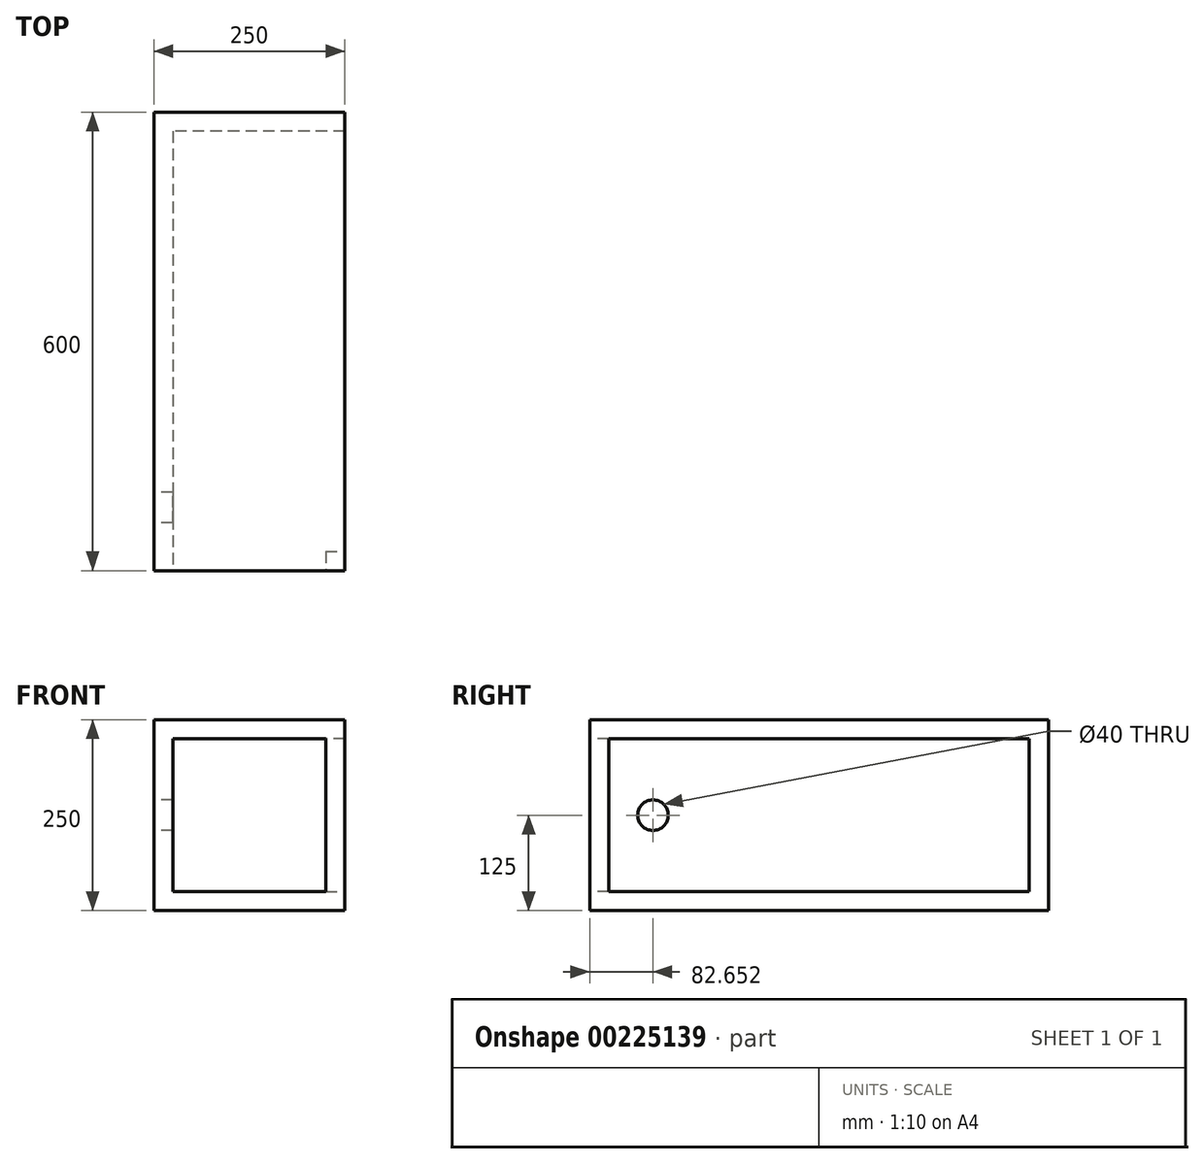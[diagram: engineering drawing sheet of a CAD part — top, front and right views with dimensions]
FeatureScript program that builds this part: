
annotation { "Feature Type Name" : "Feature", "Feature Type Description" : "" }
export const myFeature = defineFeature(function(context is Context, id is Id, definition is map)
    precondition{}
    {
        {
            var Q0;
            Q0=qCreatedBy(makeId("Front.planeOp"),FACE);
            var sketch = newSketch(context, id + "F0", { "sketchPlane" : qUnion([Q0])});
            skLineSegment(sketch, "E0.bottom", {"start": v(125, -125) * mm, "end": v(-125, -125) * mm});
            skLineSegment(sketch, "E0.top", {"start": v(125, 125) * mm, "end": v(-125, 125) * mm});
            skLineSegment(sketch, "E0.left", {"start": v(125, -125) * mm, "end": v(125, 125) * mm});
            skLineSegment(sketch, "E0.right", {"start": v(-125, -125) * mm, "end": v(-125, 125) * mm});
            skPoint(sketch, "E0.middle", {"position": v(0, 0) * mm});
            skSolve(sketch);
        }
        {
            var Q0;
            Q0=makeQuery(id+"F0.imprint","IMPRINT",FACE,{"disambiguationData":[TD([[makeQuery(id+"F0.imprint","IMPRINT",EDGE,{"derivedFrom":sQuery(id+"F0.wireOp",EDGE,"E0.bottom")}),-1.0]])]});
            extrude(context, id + "F1", {"entities" : qUnion([Q0]), "oppositeDirection" : true, "depth" : 600 * mm});
        }
        {
            var Q0;
            Q0=makeQuery(id+"F1.opExtrude","CAP_FACE",FACE,{"disambiguationData":[OSD([sQuery(id+"F0.wireOp",EDGE,"E0.bottom"),sQuery(id+"F0.wireOp",EDGE,"E0.top"),sQuery(id+"F0.wireOp",EDGE,"E0.left"),sQuery(id+"F0.wireOp",EDGE,"E0.right")])],"isStart":true});
            var sketch = newSketch(context, id + "F2", { "sketchPlane" : qUnion([Q0])});
            skLineSegment(sketch, "E1.bottom", {"start": v(100, 100) * mm, "end": v(-100, 100) * mm});
            skLineSegment(sketch, "E1.top", {"start": v(100, -100) * mm, "end": v(-100, -100) * mm});
            skLineSegment(sketch, "E1.left", {"start": v(100, 100) * mm, "end": v(100, -100) * mm});
            skLineSegment(sketch, "E1.right", {"start": v(-100, 100) * mm, "end": v(-100, -100) * mm});
            skPoint(sketch, "E1.middle", {"position": v(0, 0) * mm});
            skSolve(sketch);
        }
        {
            var Q0;
            Q0=makeQuery(id+"F2.imprint","IMPRINT",FACE,{"disambiguationData":[TD([[makeQuery(id+"F2.imprint","IMPRINT",EDGE,{"derivedFrom":sQuery(id+"F2.wireOp",EDGE,"E1.bottom")}),1.0]])]});
            extrude(context, id + "F3", {"entities" : qUnion([Q0]), "operationType" : NewBodyOperationType.REMOVE, "oppositeDirection" : true, "depth" : 575 * mm});
        }
        {
            var Q0;
            Q0=makeQuery(id+"F1.opExtrude","SWEPT_FACE",FACE,{"disambiguationData":[OSD([sQuery(id+"F0.wireOp",EDGE,"E0.left")])]});
            var sketch = newSketch(context, id + "F4", { "sketchPlane" : qUnion([Q0])});
            skLineSegment(sketch, "E2.bottom", {"start": v(25, -100) * mm, "end": v(575, -100) * mm});
            skLineSegment(sketch, "E2.top", {"start": v(25, 100) * mm, "end": v(575, 100) * mm});
            skLineSegment(sketch, "E2.left", {"start": v(25, -100) * mm, "end": v(25, 100) * mm});
            skLineSegment(sketch, "E2.right", {"start": v(575, -100) * mm, "end": v(575, 100) * mm});
            skPoint(sketch, "E2.middle", {"position": v(300, 0) * mm});
            skSolve(sketch);
        }
        {
            var Q0;
            Q0=makeQuery(id+"F4.imprint","IMPRINT",FACE,{"disambiguationData":[TD([[makeQuery(id+"F4.imprint","IMPRINT",EDGE,{"derivedFrom":sQuery(id+"F4.wireOp",EDGE,"E2.bottom")}),1.0]])]});
            extrude(context, id + "F5", {"entities" : qUnion([Q0]), "operationType" : NewBodyOperationType.REMOVE, "oppositeDirection" : true, "depth" : 48 * mm});
        }
        {
            var Q0;
            Q0=makeQuery(id+"F1.opExtrude","SWEPT_FACE",FACE,{"disambiguationData":[OSD([sQuery(id+"F0.wireOp",EDGE,"E0.right")])]});
            var sketch = newSketch(context, id + "F6", { "sketchPlane" : qUnion([Q0])});
            skPoint(sketch, "E3", {"position": v(-82.65, 0) * mm});
            skSolve(sketch);
        }
        {
            var Q0;
            Q0=sQuery(id+"F6.wireOp",VERTEX,"E3");
            var Q1;
            Q1=makeQuery(id+"F1.opExtrude","SWEPT_BODY",BODY,{"disambiguationData":[OSD([sQuery(id+"F0.wireOp",EDGE,"E0.bottom"),sQuery(id+"F0.wireOp",EDGE,"E0.top"),sQuery(id+"F0.wireOp",EDGE,"E0.left"),sQuery(id+"F0.wireOp",EDGE,"E0.right")])]});
            hole(context, id + "F7", {"style" : HoleStyle.SIMPLE, "endStyle" : HoleEndStyle.BLIND, "holeDiameter" : 40 * mm, "holeDepth" : 25 * mm, "locations" : qUnion([Q0]), "scope" : qUnion([Q1])});
        }
    });
